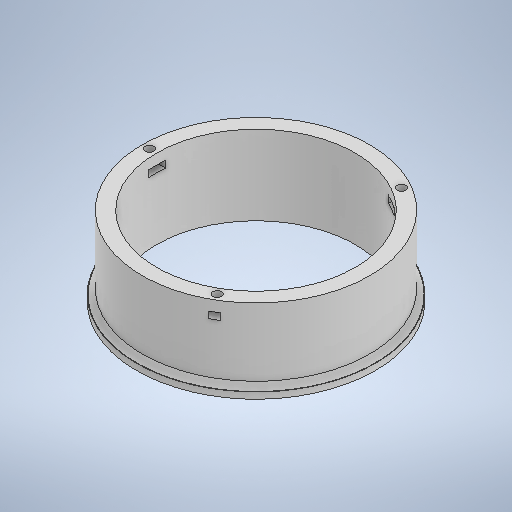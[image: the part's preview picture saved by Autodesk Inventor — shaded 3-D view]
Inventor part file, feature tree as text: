
AUTODESK INVENTOR PART (.ipt)
format: ipt  version: 2025 (Build 290162000, 162)  size: 296,960 bytes
history: native  units: mm
features: sketch x5, extrude x4, pattern_circular x2, hole x1, chamfer x1
ambient origin geometry x8: Origin, YZ Plane, XZ Plane, XY Plane, X Axis, Y Axis, Z Axis, Center Point
bodies: Solid1 (feature_tree)
feature tree (13):
  extrude  "Base"  Depth=30.0mm TaperAngle=0.0deg
  extrude  "Nut Seat"  Depth=108.9mm
  pattern_circular  "Circular Pattern1"  Count=3 Angle=360.0deg
  extrude  "Top Slice"  Depth=3.0mm
  hole  "Hole1"  [1 undecoded]
  pattern_circular  "Circular Pattern2"  [2 undecoded]
  extrude  "Lip"  Depth=3.0mm TaperAngle=45.0deg
  chamfer  "Chamfer 1"  Distance=0.5mm
  sketch  "Sketch1"  dims[d0=102.0mm d3=30.0mm d4=0.0mm]
  sketch  "Sketch2"  dims[d6=95.1mm d7=108.9mm]
  sketch  "Sketch3"  dims[d8=3.2mm d9=0.0mm d10=30.0mm d11=360.0deg]
  sketch  "Sketch4"  dims[d13=5.0mm d14=0.0mm]
  sketch  "Sketch5"  dims[d15=4.2mm d16=6.0mm d17=4.0mm d18=2.0mm d19=90.0deg d20=8.0mm d21=0.0mm d22=51.0mm d23=30.0mm d24=360.0deg d26=3.0mm d27=0.0mm d31=2.5mm d32=2.0mm d33=45.0deg d12=0.5mm]
note: 3 required parameter values undecoded (feature->parameter linkage not recoverable at this tier; creation-order binding heuristic only, values carry confidence <= 0.55)
